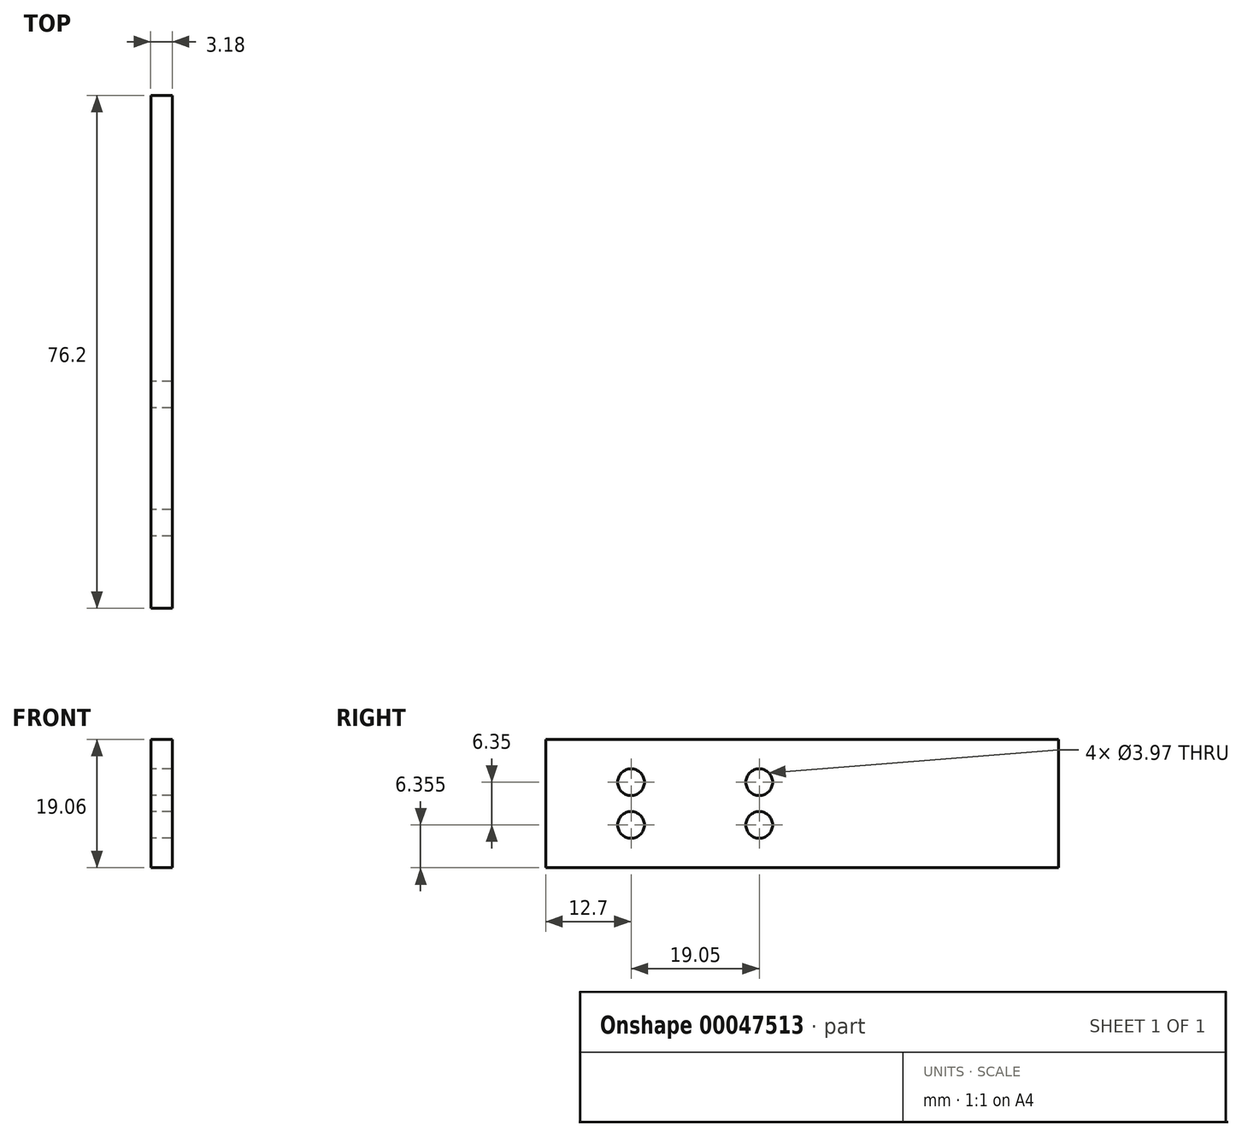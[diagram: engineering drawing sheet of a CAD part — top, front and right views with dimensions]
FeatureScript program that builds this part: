
annotation { "Feature Type Name" : "Feature", "Feature Type Description" : "" }
export const myFeature = defineFeature(function(context is Context, id is Id, definition is map)
    precondition{}
    {
        {
            var Q0;
            Q0=qCreatedBy(makeId("Front.planeOp"),FACE);
            var sketch = newSketch(context, id + "F0", { "sketchPlane" : qUnion([Q0])});
            skLineSegment(sketch, "E0.rect.bottom", {"start": v(-1.59, 9.53) * mm, "end": v(1.59, 9.53) * mm});
            skLineSegment(sketch, "E0.rect.top", {"start": v(-1.59, -9.53) * mm, "end": v(1.59, -9.53) * mm});
            skLineSegment(sketch, "E0.rect.left", {"start": v(-1.59, 9.53) * mm, "end": v(-1.59, -9.53) * mm});
            skLineSegment(sketch, "E0.rect.right", {"start": v(1.59, 9.53) * mm, "end": v(1.59, -9.53) * mm});
            skPoint(sketch, "E0.rect.middle", {"position": v(0, 0) * mm});
            skSolve(sketch);
        }
        {
            var Q0;
            Q0=makeQuery(id+"F0.imprint","IMPRINT",FACE,{"disambiguationData":[TD([[makeQuery(id+"F0.imprint","IMPRINT",EDGE,{"derivedFrom":sQuery(id+"F0.wireOp",EDGE,"E0.rect.bottom")}),-1.0]])]});
            extrude(context, id + "F1", {"entities" : qUnion([Q0]), "endBound" : BoundingType.SYMMETRIC, "depth" : 76.2 * mm});
        }
        {
            var Q0;
            Q0=makeQuery(id+"F1.opExtrude","SWEPT_FACE",FACE,{"disambiguationData":[OSD([sQuery(id+"F0.wireOp",EDGE,"E0.rect.left")])]});
            var sketch = newSketch(context, id + "F2", { "sketchPlane" : qUnion([Q0])});
            skCircle(sketch, "E1", {"center": v(25.4, -3.17) * mm, "radius": 1.98 * mm});
            skSolve(sketch);
        }
        {
            var Q0;
            Q0=makeQuery(id+"F2.imprint","IMPRINT",FACE,{"disambiguationData":[TD([[makeQuery(id+"F2.imprint","IMPRINT",EDGE,{"derivedFrom":sQuery(id+"F2.wireOp",EDGE,"E1")}),-1.0]])]});
            var sketch = newSketch(context, id + "F3", { "sketchPlane" : qUnion([Q0])});
            skCircle(sketch, "E2", {"center": v(25.4, 3.18) * mm, "radius": 1.98 * mm});
            skSolve(sketch);
        }
        {
            var Q0;
            Q0=makeQuery(id+"F2.imprint","IMPRINT",FACE,{"disambiguationData":[TD([[makeQuery(id+"F2.imprint","IMPRINT",EDGE,{"derivedFrom":sQuery(id+"F2.wireOp",EDGE,"E1")}),-1.0]])]});
            var sketch = newSketch(context, id + "F4", { "sketchPlane" : qUnion([Q0])});
            skCircle(sketch, "E3", {"center": v(6.35, 3.17) * mm, "radius": 1.98 * mm});
            skSolve(sketch);
        }
        {
            var Q0;
            Q0=makeQuery(id+"F2.imprint","IMPRINT",FACE,{"disambiguationData":[TD([[makeQuery(id+"F2.imprint","IMPRINT",EDGE,{"derivedFrom":sQuery(id+"F2.wireOp",EDGE,"E1")}),-1.0]])]});
            var sketch = newSketch(context, id + "F5", { "sketchPlane" : qUnion([Q0])});
            skCircle(sketch, "E4", {"center": v(6.35, -3.18) * mm, "radius": 1.98 * mm});
            skSolve(sketch);
        }
        {
            var Q0;
            Q0=makeQuery(id+"F4.imprint","IMPRINT",FACE,{"disambiguationData":[TD([[makeQuery(id+"F4.imprint","IMPRINT",EDGE,{"derivedFrom":sQuery(id+"F4.wireOp",EDGE,"E3")}),1.0]])]});
            extrude(context, id + "F6", {"entities" : qUnion([Q0]), "operationType" : NewBodyOperationType.REMOVE, "oppositeDirection" : true, "depth" : 3.17 * mm});
        }
        {
            var Q0;
            Q0=makeQuery(id+"F5.imprint","IMPRINT",FACE,{"disambiguationData":[TD([[makeQuery(id+"F5.imprint","IMPRINT",EDGE,{"derivedFrom":sQuery(id+"F5.wireOp",EDGE,"E4")}),1.0]])]});
            extrude(context, id + "F7", {"entities" : qUnion([Q0]), "operationType" : NewBodyOperationType.REMOVE, "oppositeDirection" : true, "depth" : 3.17 * mm});
        }
        {
            var Q0;
            Q0=makeQuery(id+"F3.imprint","IMPRINT",FACE,{"disambiguationData":[TD([[makeQuery(id+"F3.imprint","IMPRINT",EDGE,{"derivedFrom":sQuery(id+"F3.wireOp",EDGE,"E2")}),1.0]])]});
            extrude(context, id + "F8", {"entities" : qUnion([Q0]), "operationType" : NewBodyOperationType.REMOVE, "oppositeDirection" : true, "depth" : 3.17 * mm});
        }
        {
            var Q0;
            Q0=makeQuery(id+"F2.imprint","IMPRINT",FACE,{"disambiguationData":[TD([[makeQuery(id+"F2.imprint","IMPRINT",EDGE,{"derivedFrom":sQuery(id+"F2.wireOp",EDGE,"E1")}),1.0]])]});
            extrude(context, id + "F9", {"entities" : qUnion([Q0]), "operationType" : NewBodyOperationType.REMOVE, "oppositeDirection" : true, "depth" : 3.17 * mm});
        }
    });
